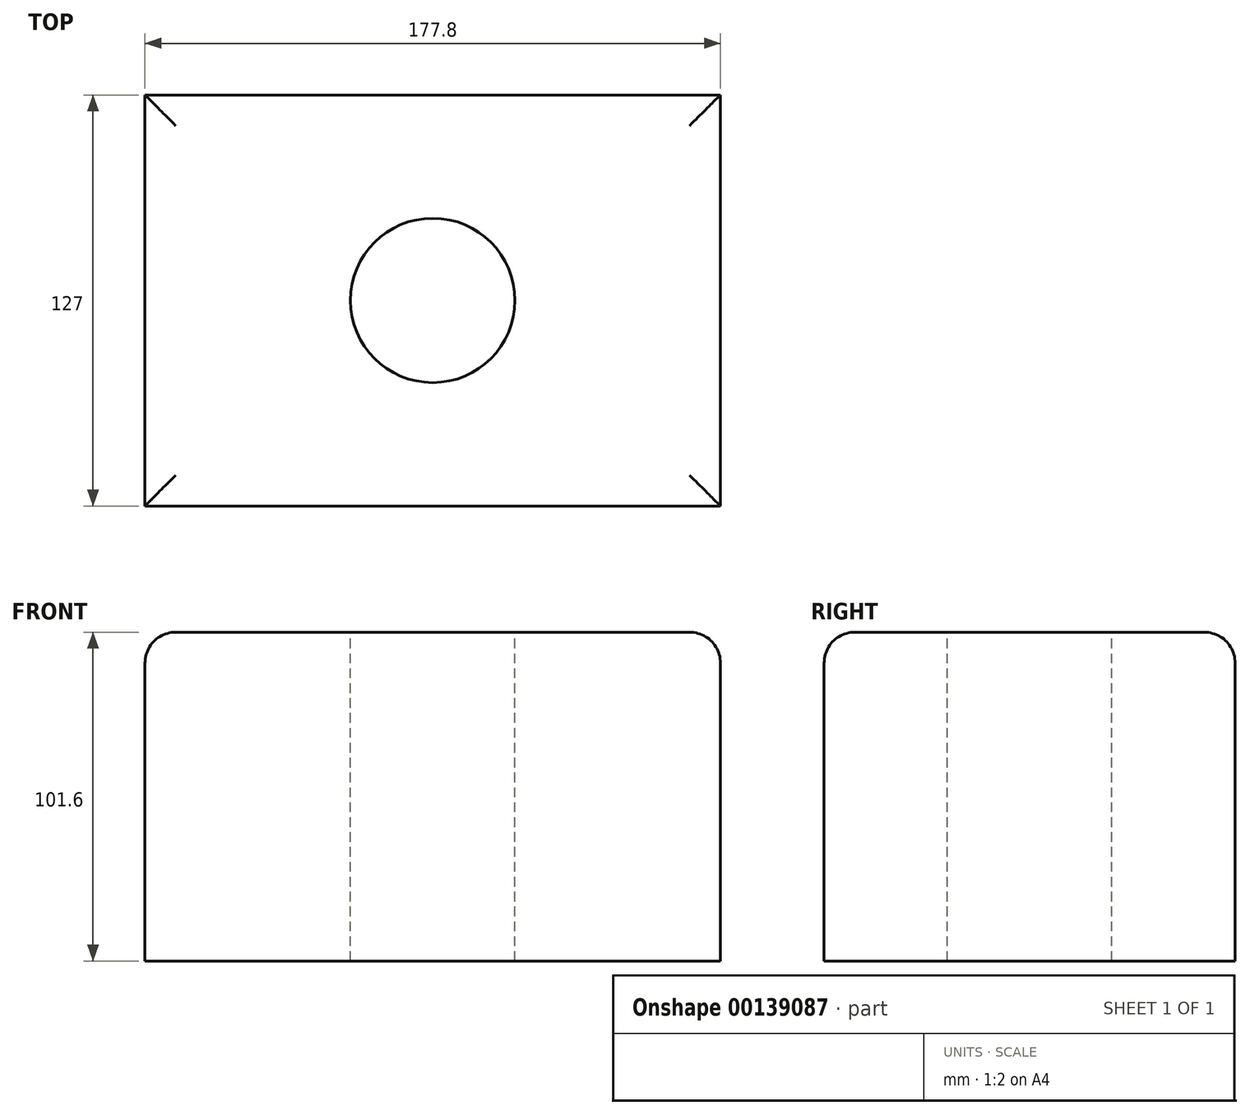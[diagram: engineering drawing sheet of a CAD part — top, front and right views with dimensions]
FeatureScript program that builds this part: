
annotation { "Feature Type Name" : "Feature", "Feature Type Description" : "" }
export const myFeature = defineFeature(function(context is Context, id is Id, definition is map)
    precondition{}
    {
        {
            var Q0;
            Q0=qCreatedBy(makeId("Top.planeOp"),FACE);
            var sketch = newSketch(context, id + "F0", { "sketchPlane" : qUnion([Q0])});
            skLineSegment(sketch, "E0.bottom", {"start": v(88.9, -63.5) * mm, "end": v(-88.9, -63.5) * mm});
            skLineSegment(sketch, "E0.top", {"start": v(88.9, 63.5) * mm, "end": v(-88.9, 63.5) * mm});
            skLineSegment(sketch, "E0.left", {"start": v(88.9, -63.5) * mm, "end": v(88.9, 63.5) * mm});
            skLineSegment(sketch, "E0.right", {"start": v(-88.9, -63.5) * mm, "end": v(-88.9, 63.5) * mm});
            skPoint(sketch, "E0.middle", {"position": v(0, 0) * mm});
            skSolve(sketch);
        }
        {
            var Q0;
            Q0 = qSketchRegion(id + "F0", true);
            extrude(context, id + "F1", {"entities" : qUnion([Q0]), "endBound" : BoundingType.SYMMETRIC, "depth" : 101.6 * mm});
        }
        {
            var Q0;
            Q0=makeQuery(id+"F1.opExtrude","CAP_FACE",FACE,{"disambiguationData":[OSD([sQuery(id+"F0.wireOp",EDGE,"E0.bottom"),sQuery(id+"F0.wireOp",EDGE,"E0.top"),sQuery(id+"F0.wireOp",EDGE,"E0.left"),sQuery(id+"F0.wireOp",EDGE,"E0.right")])],"isStart":false});
            var sketch = newSketch(context, id + "F2", { "sketchPlane" : qUnion([Q0])});
            skCircle(sketch, "E1", {"center": v(0, 0) * mm, "radius": 25.4 * mm});
            skSolve(sketch);
        }
        {
            var Q0;
            Q0 = qSketchRegion(id + "F2", true);
            extrude(context, id + "F3", {"entities" : qUnion([Q0]), "operationType" : NewBodyOperationType.REMOVE, "endBound" : BoundingType.THROUGH_ALL, "oppositeDirection" : true, "depth" : 154.44 * mm});
        }
        {
            var Q0;
            Q0=makeQuery(id+"F1.opExtrude","CAP_EDGE",EDGE,{"disambiguationData":[OSD([sQuery(id+"F0.wireOp",EDGE,"E0.bottom")])],"isStart":false});
            var Q1;
            Q1=makeQuery(id+"F1.opExtrude","CAP_EDGE",EDGE,{"disambiguationData":[OSD([sQuery(id+"F0.wireOp",EDGE,"E0.right")])],"isStart":false});
            var Q2;
            Q2=makeQuery(id+"F1.opExtrude","CAP_EDGE",EDGE,{"disambiguationData":[OSD([sQuery(id+"F0.wireOp",EDGE,"E0.left")])],"isStart":false});
            var Q3;
            Q3=makeQuery(id+"F1.opExtrude","CAP_EDGE",EDGE,{"disambiguationData":[OSD([sQuery(id+"F0.wireOp",EDGE,"E0.top")])],"isStart":false});
            fillet(context, id + "F4", {"entities" : qUnion([Q0, Q1, Q2, Q3]), "radius" : 9.52 * mm, "allowEdgeOverflow" : false});
        }
    });
